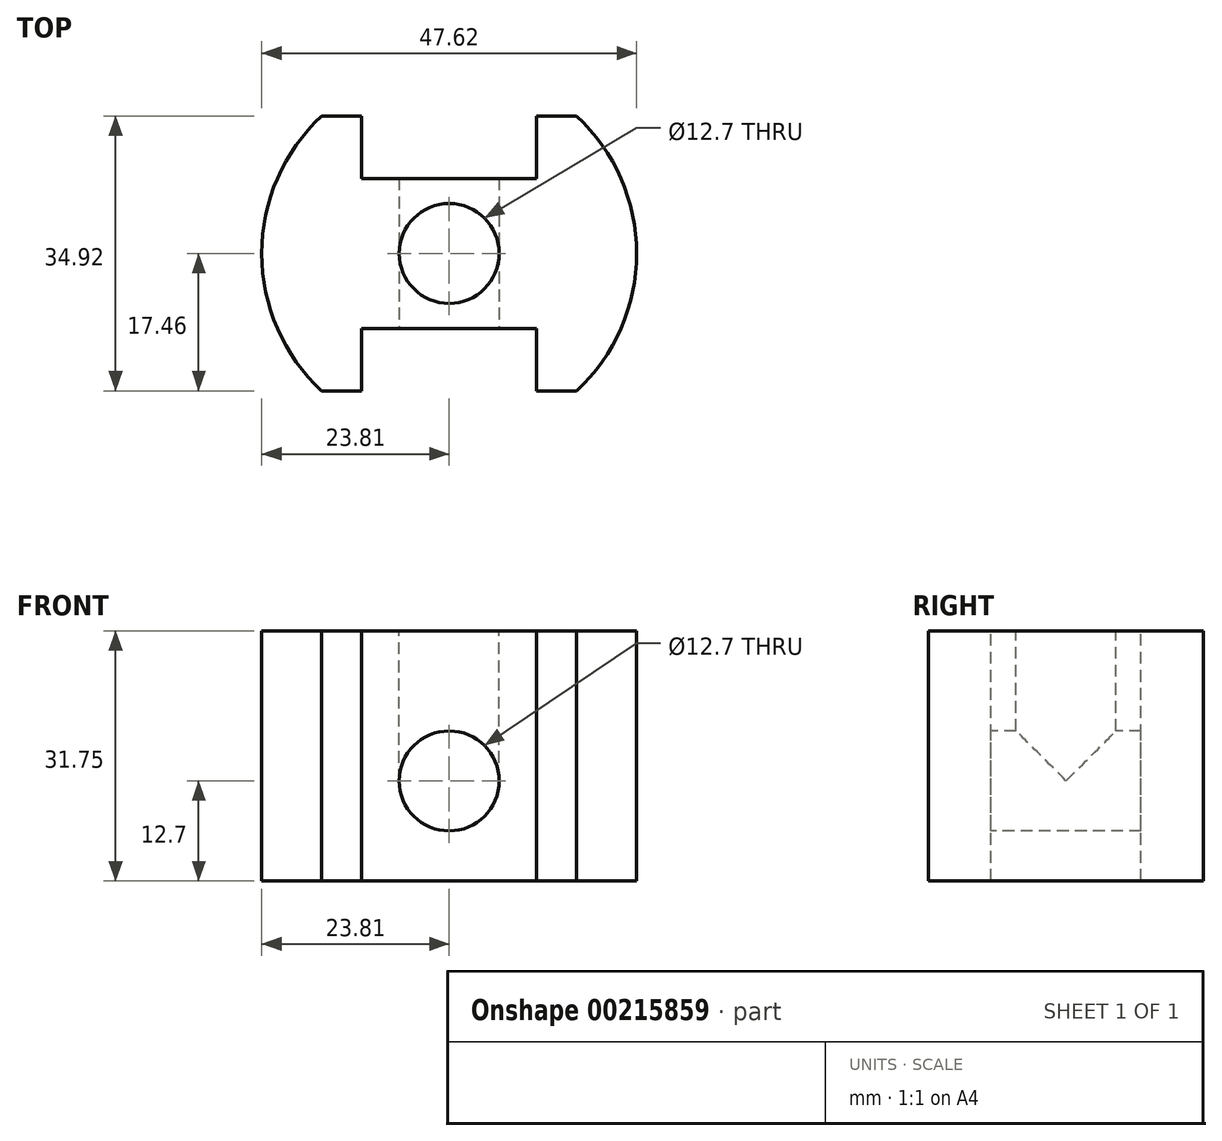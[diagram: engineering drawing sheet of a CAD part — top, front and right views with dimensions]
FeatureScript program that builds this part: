
annotation { "Feature Type Name" : "Feature", "Feature Type Description" : "" }
export const myFeature = defineFeature(function(context is Context, id is Id, definition is map)
    precondition{}
    {
        {
            var Q0;
            Q0=qCreatedBy(makeId("Top.planeOp"),FACE);
            var sketch = newSketch(context, id + "F0", { "sketchPlane" : qUnion([Q0])});
            skArc(sketch, "E0", {"start": v(-16.19, 17.46) * mm, "mid": v(-23.81, 0) * mm, "end": v(-16.19, -17.46) * mm});
            skLineSegment(sketch, "E1", {"start": v(-11.11, 17.46) * mm, "end": v(-11.11, 9.53) * mm});
            skLineSegment(sketch, "E2", {"start": v(-11.11, 9.53) * mm, "end": v(11.11, 9.53) * mm});
            skLineSegment(sketch, "E3", {"start": v(11.11, 9.53) * mm, "end": v(11.11, 17.46) * mm});
            skLineSegment(sketch, "E4.MirrorCS", {"start": v(-11.11, -9.53) * mm, "end": v(11.11, -9.53) * mm});
            skLineSegment(sketch, "E5.MirrorCS", {"start": v(11.11, -9.53) * mm, "end": v(11.11, -17.46) * mm});
            skLineSegment(sketch, "E6.MirrorCS", {"start": v(-11.11, -17.46) * mm, "end": v(-11.11, -9.53) * mm});
            skPoint(sketch, "E7", {"position": v(0, 9.53) * mm});
            skArc(sketch, "E8.trimOffspring", {"start": v(16.19, -17.46) * mm, "mid": v(23.81, 0) * mm, "end": v(16.19, 17.46) * mm});
            skLineSegment(sketch, "E9", {"start": v(-11.11, 17.46) * mm, "end": v(-16.19, 17.46) * mm});
            skPoint(sketch, "E10.orphan", {"position": v(-11.11, 21.06) * mm});
            skLineSegment(sketch, "E11.MirrorCS", {"start": v(11.11, 17.46) * mm, "end": v(16.19, 17.46) * mm});
            skLineSegment(sketch, "E12.MirrorCS", {"start": v(-11.11, -17.46) * mm, "end": v(-16.19, -17.46) * mm});
            skLineSegment(sketch, "E13.MirrorCS", {"start": v(11.11, -17.46) * mm, "end": v(16.19, -17.46) * mm});
            skPoint(sketch, "E14.orphan", {"position": v(11.11, 21.06) * mm});
            skPoint(sketch, "E15.orphan", {"position": v(11.11, -21.06) * mm});
            skPoint(sketch, "E16.orphan", {"position": v(-11.11, -21.06) * mm});
            skSolve(sketch);
        }
        {
            var Q0;
            Q0=makeQuery(id+"F0.imprint","IMPRINT",FACE,{"disambiguationData":[TD([[makeQuery(id+"F0.imprint","IMPRINT",EDGE,{"derivedFrom":sQuery(id+"F0.wireOp",EDGE,"E0")}),1.0]])]});
            extrude(context, id + "F1", {"entities" : qUnion([Q0]), "oppositeDirection" : true, "depth" : 31.75 * mm});
        }
        {
            var Q0;
            Q0=makeQuery(id+"F1.opExtrude","CAP_FACE",FACE,{"disambiguationData":[OSD([sQuery(id+"F0.wireOp",EDGE,"E0"),sQuery(id+"F0.wireOp",EDGE,"E1"),sQuery(id+"F0.wireOp",EDGE,"E2"),sQuery(id+"F0.wireOp",EDGE,"E3"),sQuery(id+"F0.wireOp",EDGE,"E4.MirrorCS"),sQuery(id+"F0.wireOp",EDGE,"E5.MirrorCS"),sQuery(id+"F0.wireOp",EDGE,"E6.MirrorCS"),sQuery(id+"F0.wireOp",EDGE,"E8.trimOffspring"),sQuery(id+"F0.wireOp",EDGE,"E9"),sQuery(id+"F0.wireOp",EDGE,"E11.MirrorCS"),sQuery(id+"F0.wireOp",EDGE,"E12.MirrorCS"),sQuery(id+"F0.wireOp",EDGE,"E13.MirrorCS")])],"isStart":true});
            var sketch = newSketch(context, id + "F2", { "sketchPlane" : qUnion([Q0])});
            skCircle(sketch, "E17", {"center": v(0, 0) * mm, "radius": 6.35 * mm});
            skSolve(sketch);
        }
        {
            var Q0;
            Q0=makeQuery(id+"F1.opExtrude","SWEPT_FACE",FACE,{"disambiguationData":[OSD([sQuery(id+"F0.wireOp",EDGE,"E4.MirrorCS")])]});
            var sketch = newSketch(context, id + "F3", { "sketchPlane" : qUnion([Q0])});
            skCircle(sketch, "E18", {"center": v(0, -19.05) * mm, "radius": 6.35 * mm});
            skSolve(sketch);
        }
        {
            var Q0;
            Q0=makeQuery(id+"F3.imprint","IMPRINT",FACE,{"disambiguationData":[TD([[makeQuery(id+"F3.imprint","IMPRINT",EDGE,{"derivedFrom":sQuery(id+"F3.wireOp",EDGE,"E18")}),1.0]])]});
            extrude(context, id + "F4", {"entities" : qUnion([Q0]), "operationType" : NewBodyOperationType.REMOVE, "endBound" : BoundingType.UP_TO_NEXT, "oppositeDirection" : true, "depth" : 25.4 * mm});
        }
        {
            var Q0;
            Q0=makeQuery(id+"F2.imprint","IMPRINT",FACE,{"disambiguationData":[TD([[makeQuery(id+"F2.imprint","IMPRINT",EDGE,{"derivedFrom":sQuery(id+"F2.wireOp",EDGE,"E17")}),1.0]])]});
            extrude(context, id + "F5", {"entities" : qUnion([Q0]), "operationType" : NewBodyOperationType.REMOVE, "endBound" : BoundingType.UP_TO_NEXT, "oppositeDirection" : true, "depth" : 25.4 * mm});
        }
    });
